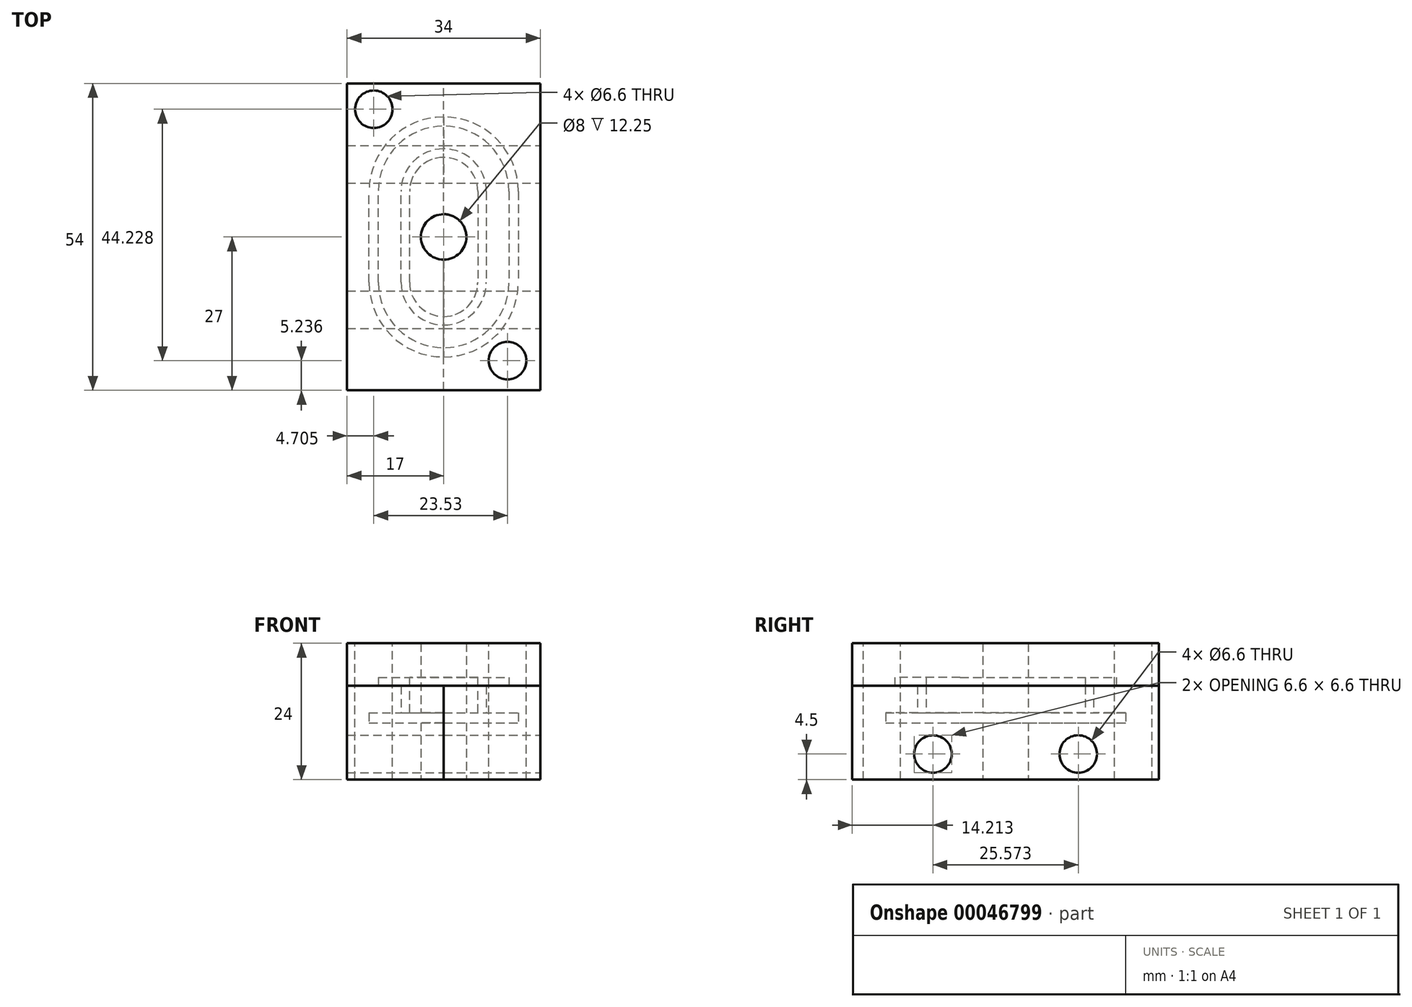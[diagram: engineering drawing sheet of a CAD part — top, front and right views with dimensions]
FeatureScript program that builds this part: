
annotation { "Feature Type Name" : "Feature", "Feature Type Description" : "" }
export const myFeature = defineFeature(function(context is Context, id is Id, definition is map)
    precondition{}
    {
        {
            var Q0;
            Q0=qCreatedBy(makeId("Right.planeOp"),FACE);
            var sketch = newSketch(context, id + "F0", { "sketchPlane" : qUnion([Q0])});
            skLineSegment(sketch, "E0.rect.bottom", {"start": v(27, -10) * mm, "end": v(-27, -10) * mm});
            skLineSegment(sketch, "E0.rect.top", {"start": v(27, 14) * mm, "end": v(-27, 14) * mm});
            skLineSegment(sketch, "E0.rect.left", {"start": v(27, -10) * mm, "end": v(27, 14) * mm});
            skLineSegment(sketch, "E0.rect.right", {"start": v(-27, -10) * mm, "end": v(-27, 14) * mm});
            skPoint(sketch, "E0.rect.middle", {"position": v(0, 2) * mm});
            skSolve(sketch);
        }
        {
            var Q0;
            Q0 = qSketchRegion(id + "F0", true);
            extrude(context, id + "F1", {"entities" : qUnion([Q0]), "oppositeDirection" : true, "depth" : 34 * mm, "symmetric" : true});
        }
        {
            var Q0;
            Q0=qCreatedBy(makeId("Front.planeOp"),FACE);
            var sketch = newSketch(context, id + "F2", { "sketchPlane" : qUnion([Q0])});
            skLineSegment(sketch, "E1", {"start": v(6, 8) * mm, "end": v(11.5, 8) * mm});
            skLineSegment(sketch, "E2", {"start": v(11.5, 8) * mm, "end": v(11.5, 6.53) * mm});
            skLineSegment(sketch, "E3", {"start": v(11.5, 6.5) * mm, "end": v(7.5, 6.5) * mm});
            skLineSegment(sketch, "E4", {"start": v(7.5, 6.5) * mm, "end": v(7.5, 1.75) * mm});
            skLineSegment(sketch, "E5", {"start": v(7.5, 1.75) * mm, "end": v(13.13, 1.75) * mm});
            skLineSegment(sketch, "E6", {"start": v(13.13, 1.75) * mm, "end": v(13.13, 0) * mm});
            skLineSegment(sketch, "E7", {"start": v(13.13, 0) * mm, "end": v(6, 0) * mm});
            skLineSegment(sketch, "E8", {"start": v(6, 0) * mm, "end": v(6, 8) * mm});
            skLineSegment(sketch, "E9", {"start": v(0, 0) * mm, "end": v(0, 21.73) * mm, "construction": true});
            skLineSegment(sketch, "E10", {"start": v(40, 6.53) * mm, "end": v(40, 6.5) * mm});
            skLineSegment(sketch, "E11", {"start": v(11.5, 6.5) * mm, "end": v(40, 6.5) * mm});
            skLineSegment(sketch, "E12", {"start": v(40, 6.53) * mm, "end": v(11.5, 6.53) * mm});
            skSolve(sketch);
        }
        {
            var Q0;
            Q0=qCreatedBy(makeId("Top.planeOp"),FACE);
            var sketch = newSketch(context, id + "F3", { "sketchPlane" : qUnion([Q0])});
            skLineSegment(sketch, "E13", {"start": v(0, 0) * mm, "end": v(0, 8) * mm, "construction": true});
            skArc(sketch, "E14.0.startCap", {"start": v(6, -8) * mm, "mid": v(0, -14) * mm, "end": v(-6, -8) * mm});
            skArc(sketch, "E14.0.endCap", {"start": v(-6, 8) * mm, "mid": v(0, 14) * mm, "end": v(6, 8) * mm});
            skLineSegment(sketch, "E14.0.left", {"start": v(-6, -8) * mm, "end": v(-6, 8) * mm});
            skLineSegment(sketch, "E15", {"start": v(0, 0) * mm, "end": v(0, -8) * mm, "construction": true});
            skLineSegment(sketch, "E16", {"start": v(6, 8) * mm, "end": v(6, 0) * mm});
            skLineSegment(sketch, "E17", {"start": v(6, 0) * mm, "end": v(6, -8) * mm});
            skSolve(sketch);
        }
        {
            var Q0;
            Q0 = qSketchRegion(id + "F2", true);
            var Q1;
            Q1=sQuery(id+"F2.wireOp",EDGE,"E7");
            var Q2;
            Q2=sQuery(id+"F2.wireOp",EDGE,"E6");
            var Q3;
            Q3=sQuery(id+"F2.wireOp",EDGE,"E5");
            var Q4;
            Q4=sQuery(id+"F2.wireOp",EDGE,"E4");
            var Q5;
            Q5=sQuery(id+"F2.wireOp",EDGE,"E3");
            var Q6;
            Q6=sQuery(id+"F2.wireOp",EDGE,"E2");
            var Q7;
            Q7=sQuery(id+"F2.wireOp",EDGE,"E1");
            var Q8;
            Q8=sQuery(id+"F2.wireOp",EDGE,"E8");
            var Q9;
            Q9 = qConstructionFilter(qBodyType(qCreatedBy(id + "F3" ,EDGE), BodyType.WIRE), ConstructionObject.NO);
            sweep(context, id + "F4", {"operationType" : NewBodyOperationType.REMOVE, "profiles" : qUnion([Q0]), "surfaceProfiles" : qUnion([Q1, Q2, Q3, Q4, Q5, Q6, Q7, Q8]), "path" : qUnion([Q9])});
        }
        {
            var Q0;
            Q0=qCreatedBy(makeId("Top.planeOp"),FACE);
            var sketch = newSketch(context, id + "F5", { "sketchPlane" : qUnion([Q0])});
            skLineSegment(sketch, "E18.0", {"start": v(-6, -8) * mm, "end": v(-6, 8) * mm});
            skArc(sketch, "E18.1", {"start": v(-6, 8) * mm, "mid": v(0, 14) * mm, "end": v(6, 8) * mm});
            skLineSegment(sketch, "E18.2", {"start": v(6, 8) * mm, "end": v(6, 0) * mm});
            skLineSegment(sketch, "E18.3", {"start": v(6, 0) * mm, "end": v(6, -8) * mm});
            skArc(sketch, "E18.4", {"start": v(6, -8) * mm, "mid": v(0, -14) * mm, "end": v(-6, -8) * mm});
            skSolve(sketch);
        }
        {
            var Q0;
            Q0 = qSketchRegion(id + "F5", true);
            var Q1;
            Q1=makeQuery(id+"F4.boolean.opBoolean","COPY",FACE,{"derivedFrom":makeQuery(id+"F4.opSweep","SWEPT_FACE",FACE,{"disambiguationData":[OSD([sQuery(id+"F2.wireOp",EDGE,"E5"),sQuery(id+"F3.wireOp",EDGE,"E16")])]})});
            extrude(context, id + "F6", {"entities" : qUnion([Q0]), "operationType" : NewBodyOperationType.REMOVE, "endBound" : BoundingType.UP_TO_SURFACE, "endBoundEntityFace" : qUnion([Q1]), "depth" : 25 * mm});
        }
        {
            var Q0;
            Q0=makeQuery(id+"F1.opExtrude","SWEPT_FACE",FACE,{"disambiguationData":[OSD([sQuery(id+"F0.wireOp",EDGE,"E0.rect.top")])]});
            var sketch = newSketch(context, id + "F7", { "sketchPlane" : qUnion([Q0])});
            skCircle(sketch, "E19", {"center": v(9, 0) * mm, "radius": 5 * mm});
            skSolve(sketch);
        }
        {
            var Q0;
            Q0=makeQuery(id+"F1.opExtrude","SWEPT_FACE",FACE,{"disambiguationData":[OSD([sQuery(id+"F0.wireOp",EDGE,"E0.rect.top")])]});
            var sketch = newSketch(context, id + "F8", { "sketchPlane" : qUnion([Q0])});
            skCircle(sketch, "E20", {"center": v(-12.3, 22.46) * mm, "radius": 3.3 * mm});
            skCircle(sketch, "E21", {"center": v(11.24, -21.76) * mm, "radius": 3.3 * mm});
            skSolve(sketch);
        }
        {
            var Q0;
            Q0 = qSketchRegion(id + "F8", true);
            extrude(context, id + "F9", {"entities" : qUnion([Q0]), "operationType" : NewBodyOperationType.REMOVE, "endBound" : BoundingType.THROUGH_ALL, "oppositeDirection" : true, "depth" : 25 * mm});
        }
        {
            var Q0;
            Q0=qCreatedBy(makeId("Right.planeOp"),FACE);
            var sketch = newSketch(context, id + "F10", { "sketchPlane" : qUnion([Q0])});
            skLineSegment(sketch, "E22", {"start": v(0, 1.75) * mm, "end": v(37.52, 1.75) * mm});
            skLineSegment(sketch, "E23", {"start": v(37.52, 1.75) * mm, "end": v(37.52, 1.78) * mm});
            skLineSegment(sketch, "E24", {"start": v(37.52, 1.78) * mm, "end": v(-38.5, 1.78) * mm});
            skLineSegment(sketch, "E25", {"start": v(-38.5, 1.78) * mm, "end": v(-38.5, 1.75) * mm});
            skLineSegment(sketch, "E26", {"start": v(-38.5, 1.75) * mm, "end": v(0, 1.75) * mm});
            skSolve(sketch);
        }
        {
            var Q0;
            Q0=makeQuery(id+"F1.opExtrude","SWEPT_FACE",FACE,{"disambiguationData":[OSD([sQuery(id+"F0.wireOp",EDGE,"E0.rect.bottom")])]});
            var sketch = newSketch(context, id + "F11", { "sketchPlane" : qUnion([Q0])});
            skPoint(sketch, "E27.rect.middle", {"position": v(0, 0) * mm});
            skLineSegment(sketch, "E28.rect.bottom", {"start": v(0.02, 30) * mm, "end": v(-0.01, 30) * mm});
            skLineSegment(sketch, "E28.rect.top", {"start": v(0.01, -30) * mm, "end": v(-0.02, -30) * mm});
            skLineSegment(sketch, "E28.rect.left", {"start": v(0.02, 30) * mm, "end": v(0.01, -30) * mm});
            skLineSegment(sketch, "E28.rect.right", {"start": v(-0.01, 30) * mm, "end": v(-0.02, -30) * mm});
            skSolve(sketch);
        }
        {
            var Q0;
            Q0 = qSketchRegion(id + "F11", true);
            var Q1;
            Q1 = qConstructionFilter(qBodyType(qCreatedBy(id + "F11" ,EDGE), BodyType.WIRE), ConstructionObject.NO);
            var Q2;
            Q2=makeQuery(id+"F4.boolean.opBoolean","COPY",FACE,{"derivedFrom":makeQuery(id+"F4.opSweep","SWEPT_FACE",FACE,{"disambiguationData":[OSD([sQuery(id+"F2.wireOp",EDGE,"E12"),sQuery(id+"F3.wireOp",EDGE,"E16")])]})});
            extrude(context, id + "F12", {"entities" : qUnion([Q0]), "operationType" : NewBodyOperationType.REMOVE, "surfaceEntities" : qUnion([Q1]), "endBound" : BoundingType.UP_TO_SURFACE, "oppositeDirection" : true, "endBoundEntityFace" : qUnion([Q2]), "depth" : 25 * mm});
        }
        {
            var Q0;
            {var subQ0=sQuery(id+"F0.wireOp",EDGE,"E0.rect.bottom");var subQ1=sQuery(id+"F0.wireOp",EDGE,"E0.rect.left");var subQ2=sQuery(id+"F0.wireOp",EDGE,"E0.rect.right");Q0=makeQuery(id+"F4.boolean.opBoolean","SPLIT",FACE,{"disambiguationData":[TD([makeQuery(id+"F1.opExtrude","SWEPT_FACE",FACE,{"disambiguationData":[OSD([subQ0])]})])],"derivedFrom":makeQuery(id+"F1.opExtrude","CAP_FACE",FACE,{"disambiguationData":[OSD([subQ0,sQuery(id+"F0.wireOp",EDGE,"E0.rect.top"),subQ1,subQ2])],"isStart":true})});}
            var sketch = newSketch(context, id + "F13", { "sketchPlane" : qUnion([Q0])});
            skCircle(sketch, "E29", {"center": v(-12.79, -5.5) * mm, "radius": 3.3 * mm});
            skCircle(sketch, "E30", {"center": v(12.79, -5.5) * mm, "radius": 3.3 * mm});
            skLineSegment(sketch, "E31", {"start": v(-12.79, -5.5) * mm, "end": v(12.79, -5.5) * mm, "construction": true});
            skLineSegment(sketch, "E32", {"start": v(0, -5.5) * mm, "end": v(0, 0) * mm, "construction": true});
            skSolve(sketch);
        }
        {
            var Q0;
            Q0 = qSketchRegion(id + "F13", true);
            extrude(context, id + "F14", {"entities" : qUnion([Q0]), "operationType" : NewBodyOperationType.REMOVE, "endBound" : BoundingType.THROUGH_ALL, "oppositeDirection" : true, "depth" : 25 * mm});
        }
        {
            var Q0;
            {var subQ0=sQuery(id+"F0.wireOp",EDGE,"E0.rect.bottom");Q0=makeQuery(id+"F12.boolean.opBoolean","SPLIT",FACE,{"disambiguationData":[TD([makeQuery(id+"F9.boolean.opBoolean","COPY",FACE,{"disambiguationData":[OD(1.0)],"derivedFrom":makeQuery(id+"F9.opExtrude","SWEPT_FACE",FACE,{"disambiguationData":[OSD([sQuery(id+"F8.wireOp",EDGE,"E21")])]})})])],"derivedFrom":makeQuery(id+"F1.opExtrude","SWEPT_FACE",FACE,{"disambiguationData":[OSD([subQ0])]})});}
            var sketch = newSketch(context, id + "F15", { "sketchPlane" : qUnion([Q0])});
            skCircle(sketch, "E33", {"center": v(0, 0) * mm, "radius": 4 * mm});
            skSolve(sketch);
        }
        {
            var Q0;
            Q0 = qSketchRegion(id + "F15", true);
            extrude(context, id + "F16", {"entities" : qUnion([Q0]), "operationType" : NewBodyOperationType.REMOVE, "oppositeDirection" : true, "depth" : 26 * mm});
        }
    });
